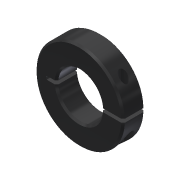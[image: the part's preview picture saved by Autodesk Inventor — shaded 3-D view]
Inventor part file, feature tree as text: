
AUTODESK INVENTOR PART (.ipt)
format: ipt  version: 2013 (Build 170138000, 138)  size: 128,512 bytes
history: native  units: in
note: dims shown in document units (in); Inventor stores cm internally (conversion verified against a paired STEP export)
features: chamfer x1, other x1, imported_body x1
ambient origin geometry x8: Origin, YZ Plane, XZ Plane, XY Plane, X Axis, Y Axis, Z Axis, Center Point
feature tree (3):
  chamfer  "Chamfer1"  [1 undecoded]
  other  "217-2736-001 Rev11"
  imported_body  "Base1"
note: 1 required parameter value undecoded (feature->parameter linkage not recoverable at this tier; creation-order binding heuristic only, values carry confidence <= 0.55)
